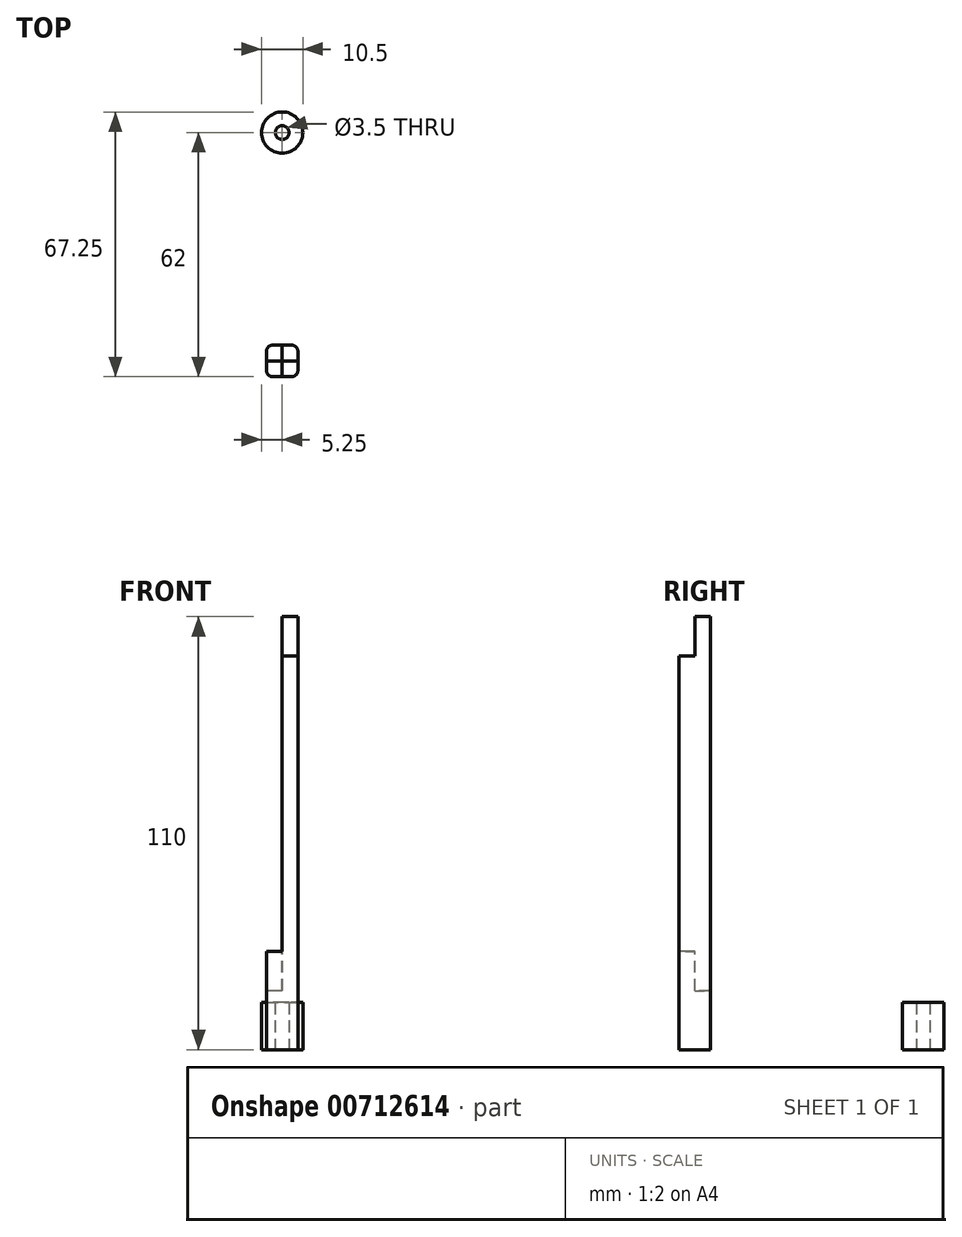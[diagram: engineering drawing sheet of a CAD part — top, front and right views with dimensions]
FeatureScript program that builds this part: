
annotation { "Feature Type Name" : "Feature", "Feature Type Description" : "" }
export const myFeature = defineFeature(function(context is Context, id is Id, definition is map)
    precondition{}
    {
        {
            var Q0;
            Q0=qCreatedBy(makeId("Top.planeOp"),FACE);
            var sketch = newSketch(context, id + "F0", { "sketchPlane" : qUnion([Q0])});
            skCircle(sketch, "E0", {"center": v(0, 0) * mm, "radius": 5.25 * mm});
            skLineSegment(sketch, "E1.bottom", {"start": v(2.5, -54) * mm, "end": v(-2.5, -54) * mm});
            skLineSegment(sketch, "E1.top", {"start": v(2.5, -4) * mm, "end": v(-2.5, -4) * mm});
            skLineSegment(sketch, "E1.left", {"start": v(2.5, -54) * mm, "end": v(2.5, -4) * mm});
            skLineSegment(sketch, "E1.right", {"start": v(-2.5, -54) * mm, "end": v(-2.5, -4) * mm});
            skPoint(sketch, "E1.middle", {"position": v(0, -29) * mm});
            skCircle(sketch, "E2", {"center": v(0, 0) * mm, "radius": 1.75 * mm});
            skLineSegment(sketch, "E3.bottom", {"start": v(2.4, -62) * mm, "end": v(-2.4, -62) * mm});
            skLineSegment(sketch, "E3.top", {"start": v(2.4, -54) * mm, "end": v(-2.4, -54) * mm});
            skLineSegment(sketch, "E3.left", {"start": v(4, -60.4) * mm, "end": v(4, -55.6) * mm});
            skLineSegment(sketch, "E3.right", {"start": v(-4, -60.4) * mm, "end": v(-4, -55.6) * mm});
            skPoint(sketch, "E3.middle", {"position": v(0, -58) * mm});
            skPoint(sketch, "E4.visualSharp", {"position": v(-4, -54) * mm});
            skArc(sketch, "E4.filletArc", {"start": v(-2.4, -54) * mm, "mid": v(-3.53, -54.47) * mm, "end": v(-4, -55.6) * mm});
            skPoint(sketch, "E5.visualSharp", {"position": v(4, -54) * mm});
            skArc(sketch, "E5.filletArc", {"start": v(4, -55.6) * mm, "mid": v(3.53, -54.47) * mm, "end": v(2.4, -54) * mm});
            skPoint(sketch, "E6.visualSharp", {"position": v(4, -62) * mm});
            skArc(sketch, "E6.filletArc", {"start": v(2.4, -62) * mm, "mid": v(3.53, -61.53) * mm, "end": v(4, -60.4) * mm});
            skPoint(sketch, "E7.visualSharp", {"position": v(-4, -62) * mm});
            skArc(sketch, "E7.filletArc", {"start": v(-4, -60.4) * mm, "mid": v(-3.53, -61.53) * mm, "end": v(-2.4, -62) * mm});
            skSolve(sketch);
        }
        {
            var Q0;
            {var subQ3=sQuery(id+"F0.wireOp",EDGE,"E3.top");Q0=makeQuery(id+"F0.imprint","IMPRINT",FACE,{"disambiguationData":[TD([[makeQuery(id+"F0.imprint","IMPRINT",EDGE,{"derivedFrom":subQ3}),-1.0]])]});}
            var Q1;
            {var subQ5=sQuery(id+"F0.wireOp",EDGE,"E1.top");Q1=makeQuery(id+"F0.imprint","IMPRINT",FACE,{"disambiguationData":[TD([[makeQuery(id+"F0.imprint","IMPRINT",EDGE,{"derivedFrom":subQ5}),1.0]])]});}
            var Q2;
            {var subQ1=sQuery(id+"F0.wireOp",EDGE,"E1.top");Q2=makeQuery(id+"F0.imprint","IMPRINT",FACE,{"disambiguationData":[TD([[makeQuery(id+"F0.imprint","IMPRINT",EDGE,{"derivedFrom":subQ1}),-1.0]])]});}
            extrude(context, id + "F1", {"entities" : qUnion([Q0, Q1, Q2]), "depth" : 12 * mm, "offsetDistance" : 25 * mm});
        }
        {
            var Q0;
            Q0=makeQuery(id+"F0.imprint","IMPRINT",FACE,{"disambiguationData":[TD([[makeQuery(id+"F0.imprint","IMPRINT",EDGE,{"derivedFrom":sQuery(id+"F0.wireOp",EDGE,"E3.bottom")}),-1.0]])]});
            var Q1;
            Q1=qSketchRegion(id+"F3",true);
            extrude(context, id + "F2", {"entities" : qUnion([Q0, Q1]), "operationType" : NewBodyOperationType.ADD, "depth" : 25 * mm, "offsetDistance" : 25 * mm});
        }
        {
            var Q0;
            Q0=makeQuery(id+"F2.opExtrude","CAP_FACE",FACE,{"disambiguationData":[OSD([sQuery(id+"F0.wireOp",EDGE,"E3.bottom"),sQuery(id+"F0.wireOp",EDGE,"E3.top"),sQuery(id+"F0.wireOp",EDGE,"E3.left"),sQuery(id+"F0.wireOp",EDGE,"E3.right"),sQuery(id+"F0.wireOp",EDGE,"E4.filletArc"),sQuery(id+"F0.wireOp",EDGE,"E5.filletArc"),sQuery(id+"F0.wireOp",EDGE,"E6.filletArc"),sQuery(id+"F0.wireOp",EDGE,"E7.filletArc")])],"isStart":false});
            var sketch = newSketch(context, id + "F3", { "sketchPlane" : qUnion([Q0])});
            skLineSegment(sketch, "E8", {"start": v(0, -54) * mm, "end": v(0, -62) * mm});
            skSolve(sketch);
        }
        {
            var Q0;
            Q0=qSketchRegion(id+"F3",true);
            var Q1;
            {var subQ2=sQuery(id+"F3.wireOp",EDGE,"E8");Q1=makeQuery(id+"F3.imprint","IMPRINT",FACE,{"disambiguationData":[TD([[makeQuery(id+"F3.imprint","IMPRINT",EDGE,{"derivedFrom":subQ2}),1.0]])]});}
            extrude(context, id + "F4", {"entities" : qUnion([Q0, Q1]), "operationType" : NewBodyOperationType.ADD, "depth" : 75 * mm, "offsetDistance" : 25 * mm});
        }
        {
            var Q0;
            Q0=makeQuery(id+"F2.opExtrude","CAP_FACE",FACE,{"disambiguationData":[OSD([sQuery(id+"F0.wireOp",EDGE,"E3.bottom"),sQuery(id+"F0.wireOp",EDGE,"E3.top"),sQuery(id+"F0.wireOp",EDGE,"E3.left"),sQuery(id+"F0.wireOp",EDGE,"E3.right"),sQuery(id+"F0.wireOp",EDGE,"E4.filletArc"),sQuery(id+"F0.wireOp",EDGE,"E5.filletArc"),sQuery(id+"F0.wireOp",EDGE,"E6.filletArc"),sQuery(id+"F0.wireOp",EDGE,"E7.filletArc")])],"isStart":false});
            var sketch = newSketch(context, id + "F5", { "sketchPlane" : qUnion([Q0])});
            skLineSegment(sketch, "E9", {"start": v(0, -58) * mm, "end": v(-4, -58) * mm});
            skSolve(sketch);
        }
        {
            var Q0;
            {var subQ3=sQuery(id+"F5.wireOp",EDGE,"E9");Q0=makeQuery(id+"F5.imprint","IMPRINT",FACE,{"disambiguationData":[TD([[makeQuery(id+"F5.imprint","IMPRINT",EDGE,{"derivedFrom":subQ3}),-1.0]])]});}
            extrude(context, id + "F6", {"entities" : qUnion([Q0]), "operationType" : NewBodyOperationType.REMOVE, "oppositeDirection" : true, "depth" : 10 * mm, "offsetDistance" : 25 * mm});
        }
        {
            var Q0;
            Q0=makeQuery(id+"F4.opExtrude","CAP_FACE",FACE,{"disambiguationData":[OSD([sQuery(id+"F0.wireOp",EDGE,"E3.bottom"),sQuery(id+"F0.wireOp",EDGE,"E3.top"),sQuery(id+"F0.wireOp",EDGE,"E3.left"),sQuery(id+"F0.wireOp",EDGE,"E5.filletArc"),sQuery(id+"F0.wireOp",EDGE,"E6.filletArc"),sQuery(id+"F3.wireOp",EDGE,"E8")])],"isStart":false});
            var sketch = newSketch(context, id + "F7", { "sketchPlane" : qUnion([Q0])});
            skLineSegment(sketch, "E10", {"start": v(4, -58) * mm, "end": v(0, -58) * mm});
            skSolve(sketch);
        }
        {
            var Q0;
            {var subQ3=sQuery(id+"F7.wireOp",EDGE,"E10");Q0=makeQuery(id+"F7.imprint","IMPRINT",FACE,{"disambiguationData":[TD([[makeQuery(id+"F7.imprint","IMPRINT",EDGE,{"derivedFrom":subQ3}),-1.0]])]});}
            extrude(context, id + "F8", {"entities" : qUnion([Q0]), "operationType" : NewBodyOperationType.ADD, "depth" : 10 * mm, "offsetDistance" : 25 * mm});
        }
    });
